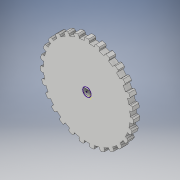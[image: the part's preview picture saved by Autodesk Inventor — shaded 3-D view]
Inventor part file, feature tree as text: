
AUTODESK INVENTOR PART (.ipt)
format: ipt  version: 2017 (Build 210142000, 142)  size: 317,440 bytes
history: native  units: in
note: dims shown in document units (in); Inventor stores cm internally (conversion verified against a paired STEP export)
features: sketch x3, extrude x2, pattern_circular x1
ambient origin geometry x8: Origin, YZ Plane, XZ Plane, XY Plane, X Axis, Y Axis, Z Axis, Center Point
bodies: Solid1 (feature_tree)
feature tree (6):
  extrude  "Extrusion1"  Depth=0.075in
  pattern_circular  "Circular Pattern1"  Count=108 Angle=360.0deg
  extrude  "Extrusion2"  Depth=0.062in
  sketch  "Sketch3"  dims[d6=0.04in d7=42.5197in d9=360.0deg d11=0.062in d12=0.062in d13=0.15in d14=0.0in d15=10.6299in d16=360.0deg d18=0.0591in d19=0.15in d20=0.0in]
  sketch  "Sketch1"  dims[d0=2.025in d4=0.075in]
  sketch  "Sketch2"  dims[d5=0.04in]
